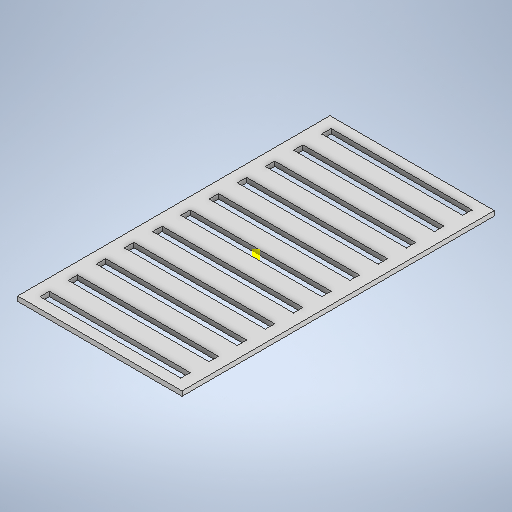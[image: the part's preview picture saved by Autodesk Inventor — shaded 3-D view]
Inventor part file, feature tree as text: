
AUTODESK INVENTOR PART (.ipt)
format: ipt  version: 2025 (Build 290162000, 162)  size: 329,216 bytes
history: native  units: in
note: dims shown in document units (in); Inventor stores cm internally (conversion verified against a paired STEP export)
features: sketch x6, extrude x4
ambient origin geometry x8: Origin, YZ Plane, XZ Plane, XY Plane, X Axis, Y Axis, Z Axis, Center Point
bodies: Solid1 (feature_tree)
feature tree (10):
  sketch  "Sketch1"  dims[d0=27.5591in d1=52.3622in]
  extrude  "Extrusion1"  Depth=52.3622in
  extrude  "Extrusion2"  Depth=1.5748in
  extrude  "Extrusion3"  TaperAngle=0.0deg  [1 undecoded]
  sketch  "Sketch5"  dims[d10=23.622in]
  sketch  "Sketch6"  dims[d11=1.5748in d12=4.7244in d13=1.5748in d14=0.0in d15=0.0in d16=23.622in d17=23.622in d18=0.0in d19=9.4488in d20=1.5748in d21=1.5748in d22=4.7244in d23=23.622in d24=9.4488in d25=1.5748in d26=4.7244in d27=1.5748in d28=4.7244in d29=1.5748in d30=23.622in d31=1.5748in d32=23.622in d33=0.0in d34=4.7244in d35=23.622in d36=0.0in d37=1.5748in d38=4.7244in d39=1.5748in d40=4.7244in d41=0.0in d42=0.0in]
  extrude  "Extrusion4"  Depth=4.7244in
  sketch  "Sketch2"  dims[d2=0.7874in d3=0.0in d4=1.5748in]
  sketch  "Sketch3"  dims[d5=23.622in d6=0.0in d7=0.0in]
  sketch  "Sketch4"  dims[d8=0.0in d9=4.7244in]
note: 1 required parameter value undecoded (feature->parameter linkage not recoverable at this tier; creation-order binding heuristic only, values carry confidence <= 0.55)
